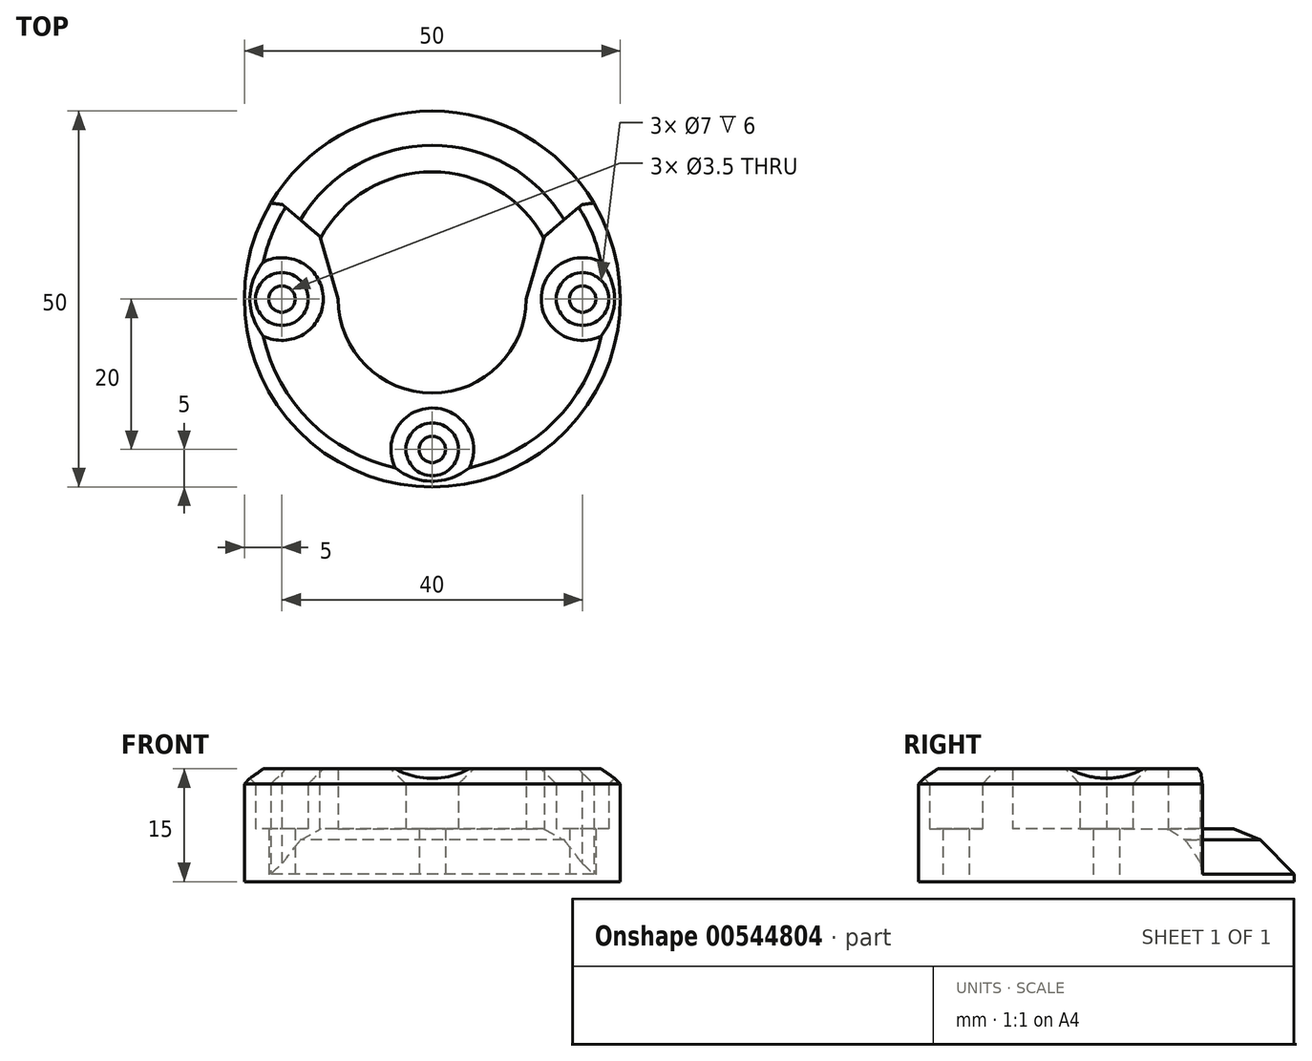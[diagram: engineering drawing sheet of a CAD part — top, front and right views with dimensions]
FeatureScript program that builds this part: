
annotation { "Feature Type Name" : "Feature", "Feature Type Description" : "" }
export const myFeature = defineFeature(function(context is Context, id is Id, definition is map)
    precondition{}
    {
        {
            var Q0;
            Q0=qCreatedBy(makeId("Top.planeOp"),FACE);
            var sketch = newSketch(context, id + "F0", { "sketchPlane" : qUnion([Q0])});
            skCircle(sketch, "E0", {"center": v(0, 0) * mm, "radius": 25 * mm});
            skLineSegment(sketch, "E1", {"start": v(-32.7, 0) * mm, "end": v(37.38, 0) * mm, "construction": true});
            skArc(sketch, "E2", {"start": v(-12.5, 0) * mm, "mid": v(0, -12.5) * mm, "end": v(12.5, 0) * mm});
            skArc(sketch, "E3", {"start": v(12.5, 0) * mm, "mid": v(0, 12.5) * mm, "end": v(-12.5, 0) * mm, "construction": true});
            skLineSegment(sketch, "E4", {"start": v(0, 0) * mm, "end": v(-17.68, 17.68) * mm, "construction": true});
            skLineSegment(sketch, "E5", {"start": v(0, 0) * mm, "end": v(17.68, 17.68) * mm, "construction": true});
            skLineSegment(sketch, "E6", {"start": v(-12.5, 0) * mm, "end": v(-17.68, 17.68) * mm});
            skLineSegment(sketch, "E7", {"start": v(12.5, 0) * mm, "end": v(17.68, 17.68) * mm});
            skCircle(sketch, "E8", {"center": v(-20, 0) * mm, "radius": 1.75 * mm});
            skCircle(sketch, "E9", {"center": v(0, -20) * mm, "radius": 1.75 * mm});
            skCircle(sketch, "E10", {"center": v(20, 0) * mm, "radius": 1.75 * mm});
            skLineSegment(sketch, "E11", {"start": v(0, 0) * mm, "end": v(0, -26.11) * mm, "construction": true});
            skCircle(sketch, "E12", {"center": v(-20, 0) * mm, "radius": 3.5 * mm});
            skCircle(sketch, "E13", {"center": v(0, -20) * mm, "radius": 3.5 * mm});
            skCircle(sketch, "E14", {"center": v(20, 0) * mm, "radius": 3.5 * mm});
            skSolve(sketch);
        }
        {
            var Q0;
            Q0=makeQuery(id+"F0.imprint","IMPRINT",FACE,{"disambiguationData":[TD([[makeQuery(id+"F0.imprint","IMPRINT",EDGE,{"derivedFrom":sQuery(id+"F0.wireOp",EDGE,"E2")}),-1.0]])]});
            extrude(context, id + "F1", {"entities" : qUnion([Q0]), "depth" : 15 * mm, "offsetDistance" : 25 * mm});
        }
        {
            var Q0;
            Q0=makeQuery(id+"F0.imprint","IMPRINT",FACE,{"disambiguationData":[TD([[makeQuery(id+"F0.imprint","IMPRINT",EDGE,{"derivedFrom":sQuery(id+"F0.wireOp",EDGE,"E2")}),1.0]])]});
            var Q1;
            Q1=makeQuery(id+"F0.imprint","IMPRINT",FACE,{"disambiguationData":[TD([[makeQuery(id+"F0.imprint","IMPRINT",EDGE,{"derivedFrom":sQuery(id+"F0.wireOp",EDGE,"E8")}),-1.0]])]});
            var Q2;
            Q2=makeQuery(id+"F0.imprint","IMPRINT",FACE,{"disambiguationData":[TD([[makeQuery(id+"F0.imprint","IMPRINT",EDGE,{"derivedFrom":sQuery(id+"F0.wireOp",EDGE,"E9")}),-1.0]])]});
            var Q3;
            Q3=makeQuery(id+"F0.imprint","IMPRINT",FACE,{"disambiguationData":[TD([[makeQuery(id+"F0.imprint","IMPRINT",EDGE,{"derivedFrom":sQuery(id+"F0.wireOp",EDGE,"E10")}),-1.0]])]});
            extrude(context, id + "F2", {"entities" : qUnion([Q0, Q1, Q2, Q3]), "operationType" : NewBodyOperationType.ADD, "depth" : 7 * mm, "offsetDistance" : 25 * mm});
        }
        {
            var Q0;
            Q0=makeQuery(id+"F2.opExtrude","CAP_EDGE",EDGE,{"disambiguationData":[OSD([sQuery(id+"F0.wireOp",EDGE,"E0")])],"isStart":false});
            chamfer(context, id + "F3", {"entities" : qUnion([Q0]), "width" : 6 * mm, "tangentPropagation" : true});
        }
        {
            var Q0;
            {var subQ0=sQuery(id+"F0.wireOp",EDGE,"E0");Q0=makeQuery(id+"F3.opChamfer","BLEND_EDGE",EDGE,{"blendedFrom":[makeQuery(id+"F2.opExtrude","CAP_EDGE",EDGE,{"disambiguationData":[OSD([subQ0])],"isStart":false}),makeQuery(id+"F2.opExtrude","CAP_FACE",FACE,{"disambiguationData":[OSD([subQ0,sQuery(id+"F0.wireOp",EDGE,"E2"),sQuery(id+"F0.wireOp",EDGE,"E6"),sQuery(id+"F0.wireOp",EDGE,"E7")])],"isStart":false})],"blendedInto":[makeQuery(id+"F2.opExtrude","CAP_FACE",FACE,{"disambiguationData":[OSD([subQ0,sQuery(id+"F0.wireOp",EDGE,"E2"),sQuery(id+"F0.wireOp",EDGE,"E6"),sQuery(id+"F0.wireOp",EDGE,"E7")])],"isStart":false})]});}
            chamfer(context, id + "F4", {"entities" : qUnion([Q0]), "width" : 5 * mm, "tangentPropagation" : true});
        }
        {
            var Q0;
            Q0=makeQuery(id+"F1.opExtrude","SWEPT_EDGE",EDGE,{"disambiguationData":[OSD([sQuery(id+"F0.wireOp",EDGE,"E0"),sQuery(id+"F0.wireOp",EDGE,"E7")])]});
            var Q1;
            Q1=makeQuery(id+"F1.opExtrude","SWEPT_EDGE",EDGE,{"disambiguationData":[OSD([sQuery(id+"F0.wireOp",EDGE,"E0"),sQuery(id+"F0.wireOp",EDGE,"E6")])]});
            chamfer(context, id + "F5", {"entities" : qUnion([Q0, Q1]), "width" : 3 * mm, "tangentPropagation" : true});
        }
        {
            var Q0;
            {var subQ0=sQuery(id+"F0.wireOp",EDGE,"E6");Q0=makeQuery(id+"F5.opChamfer","BLEND_EDGE",EDGE,{"blendedFrom":[makeQuery(id+"F1.opExtrude","SWEPT_EDGE",EDGE,{"disambiguationData":[OSD([sQuery(id+"F0.wireOp",EDGE,"E0"),subQ0])]}),makeQuery(id+"F1.opExtrude","SWEPT_FACE",FACE,{"disambiguationData":[OSD([subQ0])]})],"blendedInto":[makeQuery(id+"F1.opExtrude","SWEPT_FACE",FACE,{"disambiguationData":[OSD([subQ0])]})]});}
            var Q1;
            {var subQ0=sQuery(id+"F0.wireOp",EDGE,"E7");Q1=makeQuery(id+"F5.opChamfer","BLEND_EDGE",EDGE,{"blendedFrom":[makeQuery(id+"F1.opExtrude","SWEPT_EDGE",EDGE,{"disambiguationData":[OSD([sQuery(id+"F0.wireOp",EDGE,"E0"),subQ0])]}),makeQuery(id+"F1.opExtrude","SWEPT_FACE",FACE,{"disambiguationData":[OSD([subQ0])]})],"blendedInto":[makeQuery(id+"F1.opExtrude","SWEPT_FACE",FACE,{"disambiguationData":[OSD([subQ0])]})]});}
            chamfer(context, id + "F6", {"entities" : qUnion([Q0, Q1]), "width" : 6 * mm, "tangentPropagation" : true});
        }
        {
            var Q0;
            Q0=makeQuery(id+"F1.opExtrude","CAP_EDGE",EDGE,{"disambiguationData":[OSD([sQuery(id+"F0.wireOp",EDGE,"E0")])],"isStart":false});
            var Q1;
            Q1=makeQuery(id+"F1.opExtrude","CAP_EDGE",EDGE,{"disambiguationData":[OSD([sQuery(id+"F0.wireOp",EDGE,"E12")])],"isStart":false});
            var Q2;
            Q2=makeQuery(id+"F1.opExtrude","CAP_EDGE",EDGE,{"disambiguationData":[OSD([sQuery(id+"F0.wireOp",EDGE,"E13")])],"isStart":false});
            var Q3;
            Q3=makeQuery(id+"F1.opExtrude","CAP_EDGE",EDGE,{"disambiguationData":[OSD([sQuery(id+"F0.wireOp",EDGE,"E14")])],"isStart":false});
            chamfer(context, id + "F7", {"entities" : qUnion([Q0, Q1, Q2, Q3]), "width" : 2 * mm, "tangentPropagation" : true});
        }
    });
